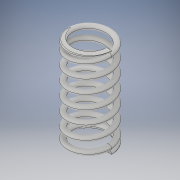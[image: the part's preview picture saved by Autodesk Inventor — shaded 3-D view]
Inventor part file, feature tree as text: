
AUTODESK INVENTOR PART (.ipt)
format: ipt  version: 2018 (Build 220112000, 112)  size: 699,904 bytes
history: native  units: in
note: dims shown in document units (in); Inventor stores cm internally (conversion verified against a paired STEP export)
features: extrude x1
ambient origin geometry x8: Origin, YZ Plane, XZ Plane, XY Plane, X Axis, Y Axis, Z Axis, Center Point
bodies: Solid1 (feature_tree)
feature tree (1):
  extrude  "Extrude1"  [1 undecoded]
note: 1 required parameter value undecoded (feature->parameter linkage not recoverable at this tier; creation-order binding heuristic only, values carry confidence <= 0.55)
